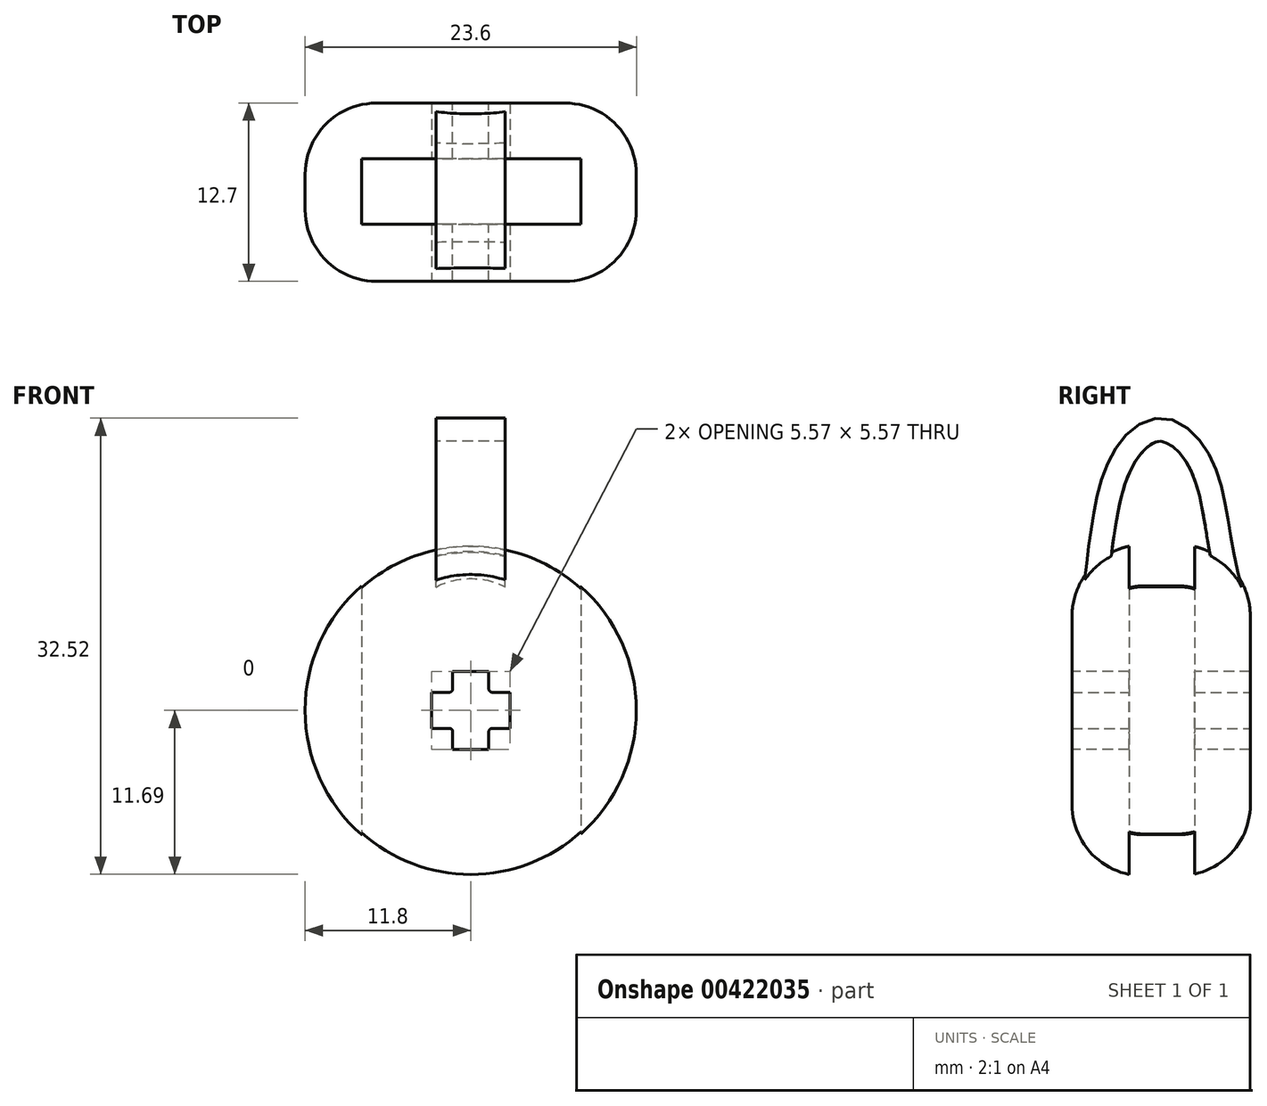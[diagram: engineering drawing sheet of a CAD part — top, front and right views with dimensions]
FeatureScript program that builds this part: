
annotation { "Feature Type Name" : "Feature", "Feature Type Description" : "" }
export const myFeature = defineFeature(function(context is Context, id is Id, definition is map)
    precondition{}
    {
        {
            var Q0;
            Q0=qCreatedBy(makeId("Front.planeOp"),FACE);
            var sketch = newSketch(context, id + "F0", { "sketchPlane" : qUnion([Q0])});
            skCircle(sketch, "E0", {"center": v(0, 0) * mm, "radius": 11.8 * mm});
            skSolve(sketch);
        }
        {
            var Q0;
            Q0 = qSketchRegion(id + "F0", true);
            extrude(context, id + "F1", {"entities" : qUnion([Q0]), "depth" : 12.7 * mm});
        }
        {
            var Q0;
            Q0=qCreatedBy(makeId("Top.planeOp"),FACE);
            var sketch = newSketch(context, id + "F2", { "sketchPlane" : qUnion([Q0])});
            skLineSegment(sketch, "E1.bottom", {"start": v(7.84, -8.63) * mm, "end": v(-7.78, -8.63) * mm});
            skLineSegment(sketch, "E1.top", {"start": v(7.84, -3.96) * mm, "end": v(-7.78, -3.96) * mm});
            skLineSegment(sketch, "E1.left", {"start": v(7.84, -8.63) * mm, "end": v(7.84, -3.96) * mm});
            skLineSegment(sketch, "E1.right", {"start": v(-7.78, -8.63) * mm, "end": v(-7.78, -3.96) * mm});
            skSolve(sketch);
        }
        {
            var Q0;
            Q0 = qSketchRegion(id + "F2", true);
            extrude(context, id + "F3", {"entities" : qUnion([Q0]), "operationType" : NewBodyOperationType.REMOVE, "endBound" : BoundingType.SYMMETRIC, "depth" : 30.99 * mm});
        }
        {
            var Q0;
            Q0=qCreatedBy(makeId("Top.planeOp"),FACE);
            cPlane(context, id + "F4", {"entities" : qUnion([Q0]), "cplaneType" : CPlaneType.OFFSET, "offset" : 10.67 * mm, "width" : 152.4 * mm, "height" : 152.4 * mm});
        }
        {
            var Q0;
            Q0=qCreatedBy(makeId("Right.planeOp"),FACE);
            var sketch = newSketch(context, id + "F5", { "sketchPlane" : qUnion([Q0])});
            skFitSpline(sketch, "E2", {"points": [v(-11.1, 9.9) * mm, v(-9.43, 17.69) * mm, v(-6.36, 20.21) * mm, v(-3.27, 17.54) * mm, v(-1.54, 9.94) * mm], "startDerivative": vector(3.03, 24.94) * mm, "endDerivative": vector(6.37, -26.03) * mm});
            skSolve(sketch);
        }
        {
            var Q0;
            Q0=qCreatedBy(id+"F4.planeOp",FACE);
            var sketch = newSketch(context, id + "F6", { "sketchPlane" : qUnion([Q0])});
            skLineSegment(sketch, "E3.bottom", {"start": v(2.45, -1.07) * mm, "end": v(-2.49, -1.07) * mm});
            skLineSegment(sketch, "E3.top", {"start": v(2.45, -2.79) * mm, "end": v(-2.49, -2.79) * mm});
            skLineSegment(sketch, "E3.left", {"start": v(2.45, -1.07) * mm, "end": v(2.45, -2.79) * mm});
            skLineSegment(sketch, "E3.right", {"start": v(-2.49, -1.07) * mm, "end": v(-2.49, -2.79) * mm});
            skSolve(sketch);
        }
        {
            var Q0;
            Q0 = qSketchRegion(id + "F6", true);
            var Q1;
            Q1 = qConstructionFilter(qBodyType(qCreatedBy(id + "F5" ,EDGE), BodyType.WIRE), ConstructionObject.NO);
            sweep(context, id + "F7", {"operationType" : NewBodyOperationType.ADD, "profiles" : qUnion([Q0]), "path" : qUnion([Q1])});
        }
        {
            var Q0;
            Q0=makeQuery(id+"F1.opExtrude","CAP_EDGE",EDGE,{"disambiguationData":[OSD([sQuery(id+"F0.wireOp",EDGE,"E0")])],"isStart":true});
            fillet(context, id + "F8", {"entities" : qUnion([Q0]), "radius" : 5.08 * mm, "tangentPropagation" : true, "allowEdgeOverflow" : false});
        }
        {
            var Q0;
            Q0=makeQuery(id+"F1.opExtrude","CAP_EDGE",EDGE,{"disambiguationData":[OSD([sQuery(id+"F0.wireOp",EDGE,"E0")])],"isStart":false});
            fillet(context, id + "F9", {"entities" : qUnion([Q0]), "radius" : 5.08 * mm, "tangentPropagation" : true, "allowEdgeOverflow" : false});
        }
        {
            var Q0;
            Q0=qCreatedBy(makeId("Front.planeOp"),FACE);
            var sketch = newSketch(context, id + "F10", { "sketchPlane" : qUnion([Q0])});
            skLineSegment(sketch, "E4.bottom", {"start": v(2.78, -1.28) * mm, "end": v(-2.78, -1.28) * mm});
            skLineSegment(sketch, "E4.top", {"start": v(2.78, 1.28) * mm, "end": v(-2.78, 1.28) * mm});
            skLineSegment(sketch, "E4.left", {"start": v(2.78, -1.28) * mm, "end": v(2.78, 1.28) * mm});
            skLineSegment(sketch, "E4.right", {"start": v(-2.78, -1.28) * mm, "end": v(-2.78, 1.28) * mm});
            skLineSegment(sketch, "E5", {"start": v(-2.78, -1.28) * mm, "end": v(2.78, 1.28) * mm});
            skSolve(sketch);
        }
        {
            var Q0;
            Q0 = qSketchRegion(id + "F10", true);
            extrude(context, id + "F11", {"entities" : qUnion([Q0]), "operationType" : NewBodyOperationType.REMOVE, "endBound" : BoundingType.SYMMETRIC, "oppositeDirection" : true, "depth" : 25.4 * mm});
        }
        {
            var Q0;
            Q0=qCreatedBy(makeId("Front.planeOp"),FACE);
            var sketch = newSketch(context, id + "F12", { "sketchPlane" : qUnion([Q0])});
            skLineSegment(sketch, "E6.bottom", {"start": v(1.28, -2.78) * mm, "end": v(-1.28, -2.78) * mm});
            skLineSegment(sketch, "E6.top", {"start": v(1.28, 2.78) * mm, "end": v(-1.28, 2.78) * mm});
            skLineSegment(sketch, "E6.left", {"start": v(1.28, -2.78) * mm, "end": v(1.28, 2.78) * mm});
            skLineSegment(sketch, "E6.right", {"start": v(-1.28, -2.78) * mm, "end": v(-1.28, 2.78) * mm});
            skLineSegment(sketch, "E7", {"start": v(-1.28, -2.78) * mm, "end": v(1.28, 2.78) * mm});
            skSolve(sketch);
        }
        {
            var Q0;
            Q0 = qSketchRegion(id + "F12", true);
            extrude(context, id + "F13", {"entities" : qUnion([Q0]), "operationType" : NewBodyOperationType.REMOVE, "endBound" : BoundingType.SYMMETRIC, "oppositeDirection" : true, "depth" : 25.4 * mm});
        }
        {
            var Q0;
            Q0=makeQuery(id+"F13.boolean.opBoolean","INTERSECT",EDGE,{"derivedFrom":[makeQuery(id+"F11.boolean.opBoolean","COPY",FACE,{"disambiguationData":[TD([makeQuery(id+"F1.opExtrude","CAP_FACE",FACE,{"disambiguationData":[OSD([sQuery(id+"F0.wireOp",EDGE,"E0")])],"isStart":true})])],"derivedFrom":makeQuery(id+"F11.opExtrude","SWEPT_FACE",FACE,{"disambiguationData":[OSD([sQuery(id+"F10.wireOp",EDGE,"E4.top")])]})}),makeQuery(id+"F13.opExtrude","SWEPT_FACE",FACE,{"disambiguationData":[OSD([sQuery(id+"F12.wireOp",EDGE,"E6.left")])]})]});
            var Q1;
            Q1=makeQuery(id+"F13.boolean.opBoolean","INTERSECT",EDGE,{"derivedFrom":[makeQuery(id+"F11.boolean.opBoolean","COPY",FACE,{"disambiguationData":[TD([makeQuery(id+"F1.opExtrude","CAP_FACE",FACE,{"disambiguationData":[OSD([sQuery(id+"F0.wireOp",EDGE,"E0")])],"isStart":true})])],"derivedFrom":makeQuery(id+"F11.opExtrude","SWEPT_FACE",FACE,{"disambiguationData":[OSD([sQuery(id+"F10.wireOp",EDGE,"E4.bottom")])]})}),makeQuery(id+"F13.opExtrude","SWEPT_FACE",FACE,{"disambiguationData":[OSD([sQuery(id+"F12.wireOp",EDGE,"E6.left")])]})]});
            var Q2;
            Q2=makeQuery(id+"F13.boolean.opBoolean","INTERSECT",EDGE,{"derivedFrom":[makeQuery(id+"F11.boolean.opBoolean","COPY",FACE,{"disambiguationData":[TD([makeQuery(id+"F1.opExtrude","CAP_FACE",FACE,{"disambiguationData":[OSD([sQuery(id+"F0.wireOp",EDGE,"E0")])],"isStart":false})])],"derivedFrom":makeQuery(id+"F11.opExtrude","SWEPT_FACE",FACE,{"disambiguationData":[OSD([sQuery(id+"F10.wireOp",EDGE,"E4.bottom")])]})}),makeQuery(id+"F13.opExtrude","SWEPT_FACE",FACE,{"disambiguationData":[OSD([sQuery(id+"F12.wireOp",EDGE,"E6.right")])]})]});
            var Q3;
            Q3=makeQuery(id+"F13.boolean.opBoolean","INTERSECT",EDGE,{"derivedFrom":[makeQuery(id+"F11.boolean.opBoolean","COPY",FACE,{"disambiguationData":[TD([makeQuery(id+"F1.opExtrude","CAP_FACE",FACE,{"disambiguationData":[OSD([sQuery(id+"F0.wireOp",EDGE,"E0")])],"isStart":true})])],"derivedFrom":makeQuery(id+"F11.opExtrude","SWEPT_FACE",FACE,{"disambiguationData":[OSD([sQuery(id+"F10.wireOp",EDGE,"E4.bottom")])]})}),makeQuery(id+"F13.opExtrude","SWEPT_FACE",FACE,{"disambiguationData":[OSD([sQuery(id+"F12.wireOp",EDGE,"E6.right")])]})]});
            var Q4;
            Q4=makeQuery(id+"F13.boolean.opBoolean","INTERSECT",EDGE,{"derivedFrom":[makeQuery(id+"F11.boolean.opBoolean","COPY",FACE,{"disambiguationData":[TD([makeQuery(id+"F1.opExtrude","CAP_FACE",FACE,{"disambiguationData":[OSD([sQuery(id+"F0.wireOp",EDGE,"E0")])],"isStart":false})])],"derivedFrom":makeQuery(id+"F11.opExtrude","SWEPT_FACE",FACE,{"disambiguationData":[OSD([sQuery(id+"F10.wireOp",EDGE,"E4.top")])]})}),makeQuery(id+"F13.opExtrude","SWEPT_FACE",FACE,{"disambiguationData":[OSD([sQuery(id+"F12.wireOp",EDGE,"E6.right")])]})]});
            var Q5;
            Q5=makeQuery(id+"F13.boolean.opBoolean","INTERSECT",EDGE,{"derivedFrom":[makeQuery(id+"F11.boolean.opBoolean","COPY",FACE,{"disambiguationData":[TD([makeQuery(id+"F1.opExtrude","CAP_FACE",FACE,{"disambiguationData":[OSD([sQuery(id+"F0.wireOp",EDGE,"E0")])],"isStart":true})])],"derivedFrom":makeQuery(id+"F11.opExtrude","SWEPT_FACE",FACE,{"disambiguationData":[OSD([sQuery(id+"F10.wireOp",EDGE,"E4.top")])]})}),makeQuery(id+"F13.opExtrude","SWEPT_FACE",FACE,{"disambiguationData":[OSD([sQuery(id+"F12.wireOp",EDGE,"E6.right")])]})]});
            var Q6;
            Q6=makeQuery(id+"F13.boolean.opBoolean","INTERSECT",EDGE,{"derivedFrom":[makeQuery(id+"F11.boolean.opBoolean","COPY",FACE,{"disambiguationData":[TD([makeQuery(id+"F1.opExtrude","CAP_FACE",FACE,{"disambiguationData":[OSD([sQuery(id+"F0.wireOp",EDGE,"E0")])],"isStart":false})])],"derivedFrom":makeQuery(id+"F11.opExtrude","SWEPT_FACE",FACE,{"disambiguationData":[OSD([sQuery(id+"F10.wireOp",EDGE,"E4.top")])]})}),makeQuery(id+"F13.opExtrude","SWEPT_FACE",FACE,{"disambiguationData":[OSD([sQuery(id+"F12.wireOp",EDGE,"E6.left")])]})]});
            var Q7;
            Q7=makeQuery(id+"F13.boolean.opBoolean","INTERSECT",EDGE,{"derivedFrom":[makeQuery(id+"F11.boolean.opBoolean","COPY",FACE,{"disambiguationData":[TD([makeQuery(id+"F1.opExtrude","CAP_FACE",FACE,{"disambiguationData":[OSD([sQuery(id+"F0.wireOp",EDGE,"E0")])],"isStart":false})])],"derivedFrom":makeQuery(id+"F11.opExtrude","SWEPT_FACE",FACE,{"disambiguationData":[OSD([sQuery(id+"F10.wireOp",EDGE,"E4.bottom")])]})}),makeQuery(id+"F13.opExtrude","SWEPT_FACE",FACE,{"disambiguationData":[OSD([sQuery(id+"F12.wireOp",EDGE,"E6.left")])]})]});
            fillet(context, id + "F14", {"entities" : qUnion([Q0, Q1, Q2, Q3, Q4, Q5, Q6, Q7]), "radius" : 0.25 * mm, "tangentPropagation" : true, "allowEdgeOverflow" : false});
        }
    });
